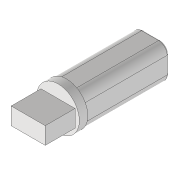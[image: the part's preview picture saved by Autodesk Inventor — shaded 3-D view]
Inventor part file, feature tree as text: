
AUTODESK INVENTOR PART (.ipt)
format: ipt  version: 2020 (Build 240168000, 168)  size: 138,240 bytes
history: native  units: mm
features: extrude x4, sketch x4, fillet x1
ambient origin geometry x8: Origin, YZ Plane, XZ Plane, XY Plane, X Axis, Y Axis, Z Axis, Center Point
bodies: Volumenkörper1 (feature_tree)
feature tree (9):
  extrude  "Extrusion1"  Depth=20.0mm
  extrude  "Extrusion2"  Depth=35.0mm
  extrude  "Extrusion3"  Depth=40.0mm
  extrude  "Extrusion4"  Depth=10.0mm
  fillet  "Rundung1"  Radius=100.0mm
  sketch  "Skizze2"  dims[d0=40.0mm d1=20.0mm]
  sketch  "Skizze3"  dims[d2=35.0mm d3=0.0mm d4=50.0mm]
  sketch  "Skizze4"  dims[d5=10.0mm d6=0.0mm d7=40.0mm]
  sketch  "Skizze5"  dims[d8=40.0mm d9=10.0mm d10=100.0mm d11=0.0mm d12=20.0mm d13=39.25mm d14=0.0mm d15=2.0mm]
